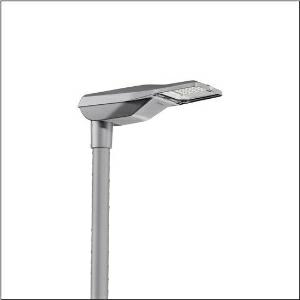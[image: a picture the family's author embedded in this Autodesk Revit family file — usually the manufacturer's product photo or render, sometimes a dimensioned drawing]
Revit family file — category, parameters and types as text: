
# Revit family: streetlight_sl_21_iq_micro___st1_0a_5xe1d41d08db_a30f
name_source: partatom
category: Lighting Fixtures
units: mm (PartAtom-declared; Revit-internal decimal feet)

## family parameters
Cut with Voids When Loaded = No
Host = Face
Light Source = No
Part Type = Normal
Room Calculation Point = No
Round Connector Dimension = Use Diameter
Shared = No

## types (1)
- --- (1 x LED, 5010 lm, 36.4 W, 4000K)
    Apparent Load = 36 VA
    CIE Flux Codes = 37 72 97 100 100
    Color Rendering = 70
    Color Temperature = 4000K
    Default Elevation = 1800 mm
    Description = Streetlight SL 21 iQ micro, mast luminaire, primary light control with lens, of PMMA, primary optical cover: cover, of toughened safety glass, transparent, light distribution: ST1.0a, light emission: direct distribution, primary light characteristic: asymmetric, installation type: post-top, side-entry, LED, High Power LED, rated luminous flux: 5.010lm, luminous efficacy: 138lm/W, light colour: 740, colour temperature: 4000K, control gear: iQ-Comfort, control: Auto-Match, Temp-Guard, Lumen-Switch, Night-Set, Smart-Wire, Light-Fading, Desk-Remote (wireless, voltage-free reading and setting of iQ features in the workshop via application-optimized NFC function/RFID function), optimised constant luminous flux control (CLO 2.0), pre-setting: linear dimming characteristic, mains connection: 220..240V, AC, 50/60Hz, start of lifetime: 36W, end of service life: 38W, reduction: 16W, luminaire housing, of diecast aluminium, powder-coated, Siteco® metallic grey (DB 702S), corrosivity category C5 mid according to DIN EN ISO 12944, please order mast flange separately, inclination adjustable: 0°, 5°, 10°, 15°, sealing non-destructively replaceable, multi-level sealing system, length: 528mm, width: 235mm, height: 110mm, mast flange for spigot size: 42mm (side-entry): 5XC10008XM4, 60/48mm (side-entry/post-top): 5XC10108XM2, 76/60mm (side-entry/post-top): 5XC10108XM1, protection rating (complete): IP66, insulation class (complete): insulation class II (safety insulation), certification: CE, ENEC, ENEC+, VDE, impact resistance: IK10, permissible operating ambient temperature for outdoor applications: -40..+50°C, standard-compliant lighting for roads and squares, packaging unit: 1 piece

Light Distribution: ST1.0a
    Height = 110 mm
    Lamp = 1 x LED
    Lamp Light Flux = 5010 lm
    Lamp Power = 36.4 W
    Lamp count = 1
    Length = 528 mm
    Luminous efficacy = 138 lm/W
    Manufacturer = Siteco
    ModVariant = No
    Model = 5XE1D41D08DB
    Number of Poles = 1
    OnlyDefault = Yes
    Power Factor = 1
    Product Name = Streetlight SL 21 iQ micro | ST1.0a
    Product group = mast luminaire | pylon top
    ProductGroupID = 6100
    Protection Class = Protection class II
    Protection Degree = IP 66
    RLX_Detail_Level = 1
    RLX_Emergency_Light_Flux = 0 lm
    RLX_Emergency_Type = 0
    RLX_Emergency_Type_DB = No
    RlxData = <blob elided: 99701 chars, md5=ab8112c8>
    Socket = socket
    Standby Power = 0 W
    System Light Flux = 5010 lm
    System Power = 36 W
    Type Comments = factory setting: luminous flux: 100 % | dim-lin: 254 | 715 mA
    Type Image = l_1006881.jpg
    URL = http://relux.com
    VarID = @adj_177429
    Voltage = 0 V
    Weight = 0.00 kg
    Width = 235 mm

## geometry (parser evidence)
native form markers: Blend x4, Sweep x12
no freeform markers — native parametric forms only
